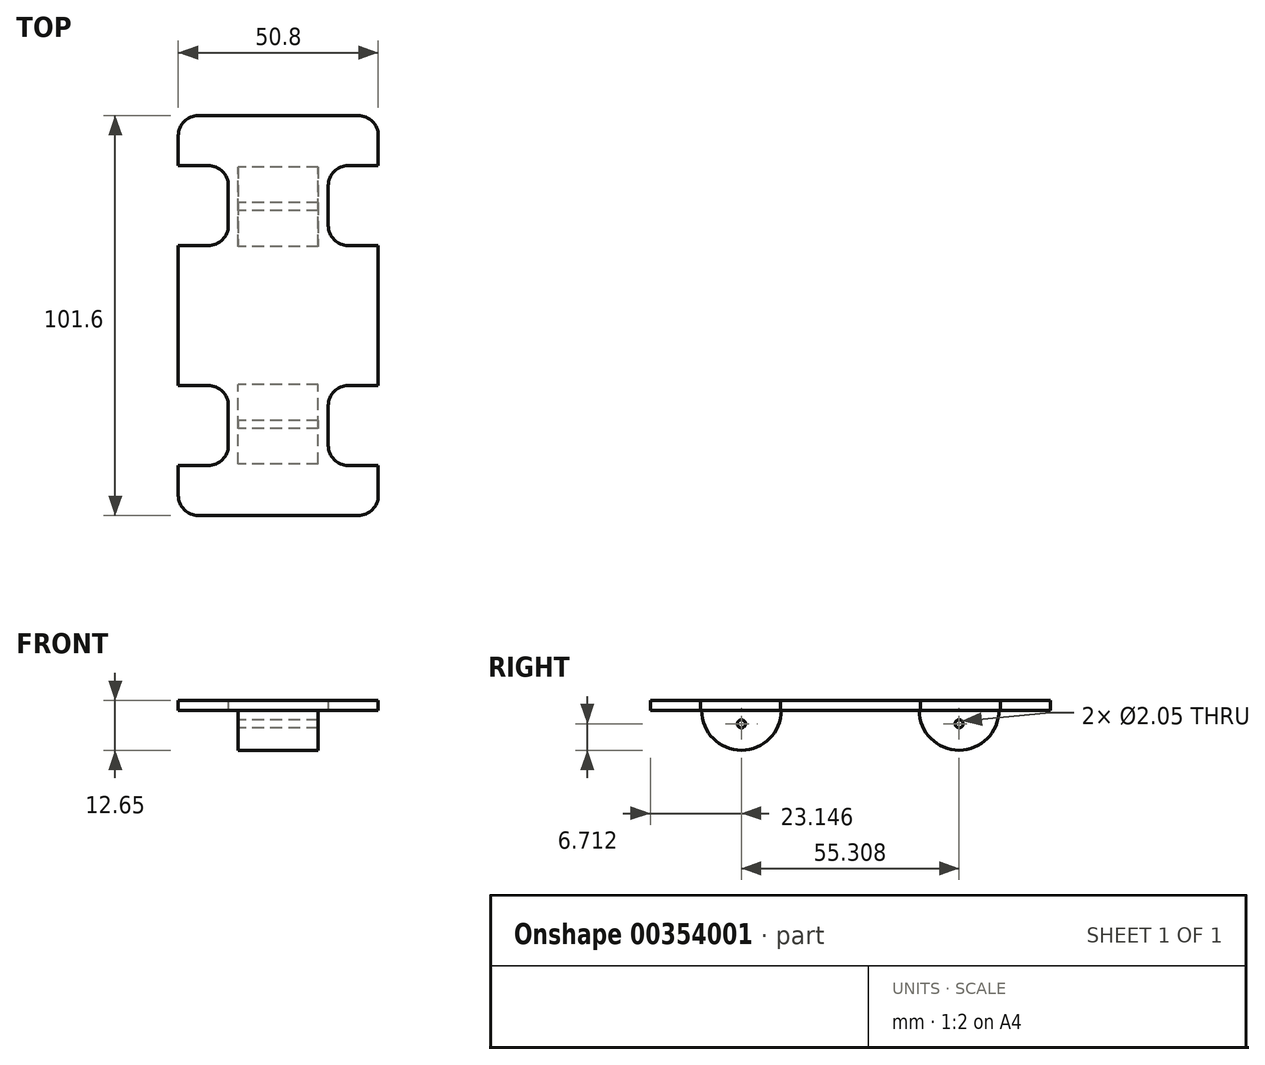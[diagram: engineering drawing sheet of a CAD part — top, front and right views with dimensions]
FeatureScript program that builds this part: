
annotation { "Feature Type Name" : "Feature", "Feature Type Description" : "" }
export const myFeature = defineFeature(function(context is Context, id is Id, definition is map)
    precondition{}
    {
        {
            var Q0;
            Q0=qCreatedBy(makeId("Top.planeOp"),FACE);
            var sketch = newSketch(context, id + "F0", { "sketchPlane" : qUnion([Q0])});
            skLineSegment(sketch, "E0.bottom", {"start": v(25.4, -50.8) * mm, "end": v(-25.4, -50.8) * mm});
            skLineSegment(sketch, "E0.top", {"start": v(25.4, 50.8) * mm, "end": v(-25.4, 50.8) * mm});
            skLineSegment(sketch, "E0.left", {"start": v(25.4, -50.8) * mm, "end": v(25.4, -38.1) * mm});
            skLineSegment(sketch, "E0.right", {"start": v(-25.4, -50.8) * mm, "end": v(-25.4, -38.1) * mm});
            skPoint(sketch, "E0.middle", {"position": v(0, 0) * mm});
            skLineSegment(sketch, "E1.bottom", {"start": v(-25.4, -38.1) * mm, "end": v(-12.7, -38.1) * mm});
            skLineSegment(sketch, "E1.top", {"start": v(-25.4, -17.78) * mm, "end": v(-12.7, -17.78) * mm});
            skLineSegment(sketch, "E1.right", {"start": v(-12.7, -38.1) * mm, "end": v(-12.7, -17.78) * mm});
            skLineSegment(sketch, "E2.MirrorCS", {"start": v(25.4, -38.1) * mm, "end": v(12.7, -38.1) * mm});
            skLineSegment(sketch, "E3.MirrorCS", {"start": v(12.7, -38.1) * mm, "end": v(12.7, -17.78) * mm});
            skLineSegment(sketch, "E4.MirrorCS", {"start": v(25.4, -17.78) * mm, "end": v(12.7, -17.78) * mm});
            skLineSegment(sketch, "E5.MirrorCS", {"start": v(25.4, 17.78) * mm, "end": v(12.7, 17.78) * mm});
            skLineSegment(sketch, "E6.MirrorCS", {"start": v(12.7, 38.1) * mm, "end": v(12.7, 17.78) * mm});
            skLineSegment(sketch, "E7.MirrorCS", {"start": v(25.4, 38.1) * mm, "end": v(12.7, 38.1) * mm});
            skLineSegment(sketch, "E8.MirrorCS", {"start": v(-25.4, 17.78) * mm, "end": v(-12.7, 17.78) * mm});
            skLineSegment(sketch, "E9.MirrorCS", {"start": v(-12.7, 38.1) * mm, "end": v(-12.7, 17.78) * mm});
            skLineSegment(sketch, "E10.MirrorCS", {"start": v(-25.4, 38.1) * mm, "end": v(-12.7, 38.1) * mm});
            skLineSegment(sketch, "E11.trimOffspring", {"start": v(-25.4, 38.1) * mm, "end": v(-25.4, 50.8) * mm});
            skLineSegment(sketch, "E12.trimOffspring", {"start": v(25.4, 38.1) * mm, "end": v(25.4, 50.8) * mm});
            skLineSegment(sketch, "E13.trimOffspring", {"start": v(25.4, -17.78) * mm, "end": v(25.4, 17.78) * mm});
            skLineSegment(sketch, "E14.trimOffspring", {"start": v(-25.4, -17.78) * mm, "end": v(-25.4, 17.78) * mm});
            skSolve(sketch);
        }
        {
            var Q0;
            Q0 = qSketchRegion(id + "F0", true);
            extrude(context, id + "F1", {"entities" : qUnion([Q0]), "depth" : 2.54 * mm});
        }
        {
            var Q0;
            Q0=makeQuery(id+"F1.opExtrude","SWEPT_EDGE",EDGE,{"disambiguationData":[OSD([sQuery(id+"F0.wireOp",EDGE,"E0.top"),sQuery(id+"F0.wireOp",EDGE,"E12.trimOffspring")])]});
            var Q1;
            Q1=makeQuery(id+"F1.opExtrude","SWEPT_EDGE",EDGE,{"disambiguationData":[OSD([sQuery(id+"F0.wireOp",EDGE,"E0.top"),sQuery(id+"F0.wireOp",EDGE,"E11.trimOffspring")])]});
            var Q2;
            Q2=makeQuery(id+"F1.opExtrude","SWEPT_EDGE",EDGE,{"disambiguationData":[OSD([sQuery(id+"F0.wireOp",EDGE,"E0.bottom"),sQuery(id+"F0.wireOp",EDGE,"E0.left")])]});
            var Q3;
            Q3=makeQuery(id+"F1.opExtrude","SWEPT_EDGE",EDGE,{"disambiguationData":[OSD([sQuery(id+"F0.wireOp",EDGE,"E0.bottom"),sQuery(id+"F0.wireOp",EDGE,"E0.right")])]});
            var Q4;
            Q4=makeQuery(id+"F1.opExtrude","SWEPT_EDGE",EDGE,{"disambiguationData":[OSD([sQuery(id+"F0.wireOp",EDGE,"E1.top"),sQuery(id+"F0.wireOp",EDGE,"E1.right")])]});
            var Q5;
            Q5=makeQuery(id+"F1.opExtrude","SWEPT_EDGE",EDGE,{"disambiguationData":[OSD([sQuery(id+"F0.wireOp",EDGE,"E1.bottom"),sQuery(id+"F0.wireOp",EDGE,"E1.right")])]});
            var Q6;
            Q6=makeQuery(id+"F1.opExtrude","SWEPT_EDGE",EDGE,{"disambiguationData":[OSD([sQuery(id+"F0.wireOp",EDGE,"E8.MirrorCS"),sQuery(id+"F0.wireOp",EDGE,"E9.MirrorCS")])]});
            var Q7;
            Q7=makeQuery(id+"F1.opExtrude","SWEPT_EDGE",EDGE,{"disambiguationData":[OSD([sQuery(id+"F0.wireOp",EDGE,"E9.MirrorCS"),sQuery(id+"F0.wireOp",EDGE,"E10.MirrorCS")])]});
            var Q8;
            Q8=makeQuery(id+"F1.opExtrude","SWEPT_EDGE",EDGE,{"disambiguationData":[OSD([sQuery(id+"F0.wireOp",EDGE,"E6.MirrorCS"),sQuery(id+"F0.wireOp",EDGE,"E7.MirrorCS")])]});
            var Q9;
            Q9=makeQuery(id+"F1.opExtrude","SWEPT_EDGE",EDGE,{"disambiguationData":[OSD([sQuery(id+"F0.wireOp",EDGE,"E5.MirrorCS"),sQuery(id+"F0.wireOp",EDGE,"E6.MirrorCS")])]});
            var Q10;
            Q10=makeQuery(id+"F1.opExtrude","SWEPT_EDGE",EDGE,{"disambiguationData":[OSD([sQuery(id+"F0.wireOp",EDGE,"E3.MirrorCS"),sQuery(id+"F0.wireOp",EDGE,"E4.MirrorCS")])]});
            var Q11;
            Q11=makeQuery(id+"F1.opExtrude","SWEPT_EDGE",EDGE,{"disambiguationData":[OSD([sQuery(id+"F0.wireOp",EDGE,"E2.MirrorCS"),sQuery(id+"F0.wireOp",EDGE,"E3.MirrorCS")])]});
            fillet(context, id + "F2", {"entities" : qUnion([Q0, Q1, Q2, Q3, Q4, Q5, Q6, Q7, Q8, Q9, Q10, Q11]), "radius" : 5.08 * mm, "tangentPropagation" : true, "allowEdgeOverflow" : false});
        }
        {
            var Q0;
            Q0=qCreatedBy(makeId("Right.planeOp"),FACE);
            var sketch = newSketch(context, id + "F3", { "sketchPlane" : qUnion([Q0])});
            skArc(sketch, "E15", {"start": v(17.54, 0) * mm, "mid": v(27.65, -10.11) * mm, "end": v(37.77, 0) * mm});
            skLineSegment(sketch, "E16", {"start": v(37.77, 0) * mm, "end": v(17.54, 0) * mm});
            skCircle(sketch, "E17", {"center": v(27.65, -3.4) * mm, "radius": 1.02 * mm});
            skArc(sketch, "E18.MirrorCS", {"start": v(-17.54, 0) * mm, "mid": v(-27.65, -10.11) * mm, "end": v(-37.77, 0) * mm});
            skLineSegment(sketch, "E19.MirrorCS", {"start": v(-37.77, 0) * mm, "end": v(-17.54, 0) * mm});
            skCircle(sketch, "E20.MirrorC", {"center": v(-27.65, -3.4) * mm, "radius": 1.02 * mm});
            skSolve(sketch);
        }
        {
            var Q0;
            Q0 = qSketchRegion(id + "F3", true);
            extrude(context, id + "F4", {"entities" : qUnion([Q0]), "operationType" : NewBodyOperationType.ADD, "depth" : 20.32 * mm, "symmetric" : true});
        }
    });
